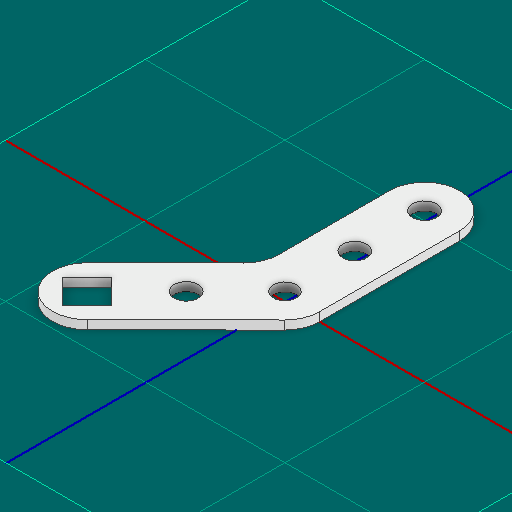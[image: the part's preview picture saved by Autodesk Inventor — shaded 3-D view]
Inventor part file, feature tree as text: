
AUTODESK INVENTOR PART (.ipt)
format: ipt  version: 2025 (Build 290162000, 162)  size: 131,072 bytes
history: native  units: in
note: dims shown in document units (in); Inventor stores cm internally (conversion verified against a paired STEP export)
features: other x3, extrude x1, sketch x1
ambient origin geometry x8: Origin, YZ Plane, XZ Plane, XY Plane, X Axis, Y Axis, Z Axis, Center Point
bodies: Solid1 (feature_tree)
feature tree (5):
  other  "Blocks"
  extrude  "Extrusion1"  Depth=0.5in
  sketch  "Sketch1"  dims[d0=0.5in d5=0.5in d6=0.25in d7=0.0625in d8=0.0in d9=0.248in d10=45.0deg d11=0.248in]
  other  "main"
  other  "main:1"
